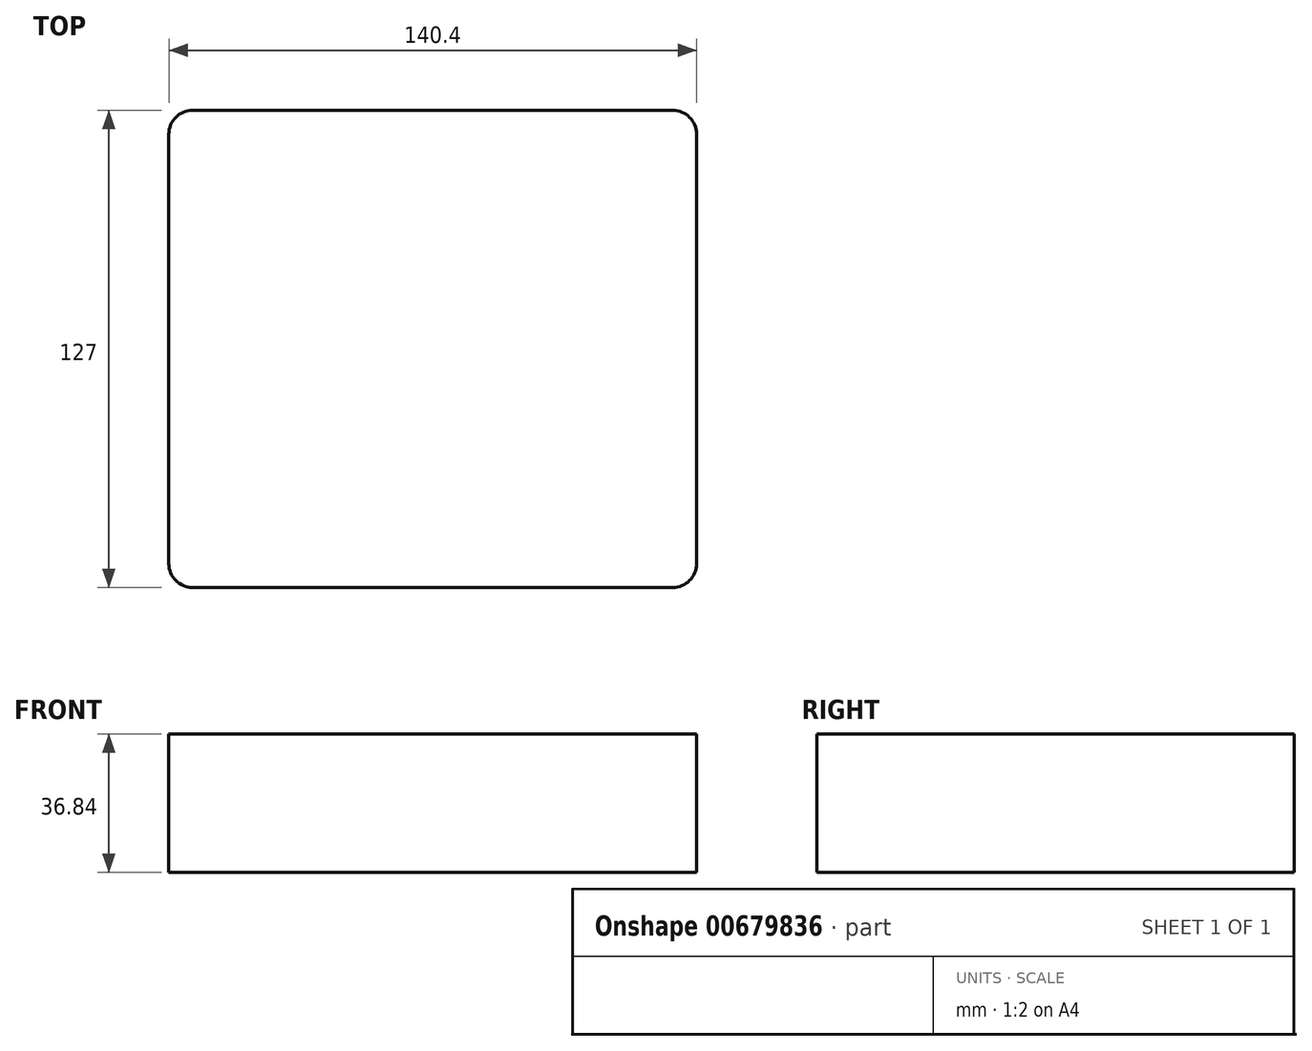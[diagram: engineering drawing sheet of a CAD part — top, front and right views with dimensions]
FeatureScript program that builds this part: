
annotation { "Feature Type Name" : "Feature", "Feature Type Description" : "" }
export const myFeature = defineFeature(function(context is Context, id is Id, definition is map)
    precondition{}
    {
        {
            var Q0;
            Q0=qCreatedBy(makeId("Front.planeOp"),FACE);
            var sketch = newSketch(context, id + "F0", { "sketchPlane" : qUnion([Q0])});
            skLineSegment(sketch, "E0.bottom", {"start": v(-70.2, 18.42) * mm, "end": v(70.2, 18.42) * mm});
            skLineSegment(sketch, "E0.top", {"start": v(-70.2, -18.42) * mm, "end": v(70.2, -18.42) * mm});
            skLineSegment(sketch, "E0.left", {"start": v(-70.2, 18.42) * mm, "end": v(-70.2, -18.42) * mm});
            skLineSegment(sketch, "E0.right", {"start": v(70.2, 18.42) * mm, "end": v(70.2, -18.42) * mm});
            skPoint(sketch, "E0.middle", {"position": v(0, 0) * mm});
            skSolve(sketch);
        }
        {
            var Q0;
            Q0=makeQuery(id+"F0.imprint","IMPRINT",FACE,{"disambiguationData":[TD([[makeQuery(id+"F0.imprint","IMPRINT",EDGE,{"derivedFrom":sQuery(id+"F0.wireOp",EDGE,"E0.bottom")}),-1.0]])]});
            extrude(context, id + "F1", {"entities" : qUnion([Q0]), "endBound" : BoundingType.SYMMETRIC, "depth" : 127 * mm, "offsetDistance" : 25.4 * mm});
        }
        {
            var Q0;
            Q0=makeQuery(id+"F1.opExtrude","CAP_EDGE",EDGE,{"disambiguationData":[OSD([sQuery(id+"F0.wireOp",EDGE,"E0.right")])],"isStart":false});
            var Q1;
            Q1=makeQuery(id+"F1.opExtrude","CAP_EDGE",EDGE,{"disambiguationData":[OSD([sQuery(id+"F0.wireOp",EDGE,"E0.left")])],"isStart":false});
            var Q2;
            Q2=makeQuery(id+"F1.opExtrude","CAP_EDGE",EDGE,{"disambiguationData":[OSD([sQuery(id+"F0.wireOp",EDGE,"E0.right")])],"isStart":true});
            var Q3;
            Q3=makeQuery(id+"F1.opExtrude","CAP_EDGE",EDGE,{"disambiguationData":[OSD([sQuery(id+"F0.wireOp",EDGE,"E0.left")])],"isStart":true});
            fillet(context, id + "F2", {"entities" : qUnion([Q0, Q1, Q2, Q3]), "radius" : 6.35 * mm, "tangentPropagation" : true, "allowEdgeOverflow" : false});
        }
    });
